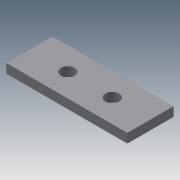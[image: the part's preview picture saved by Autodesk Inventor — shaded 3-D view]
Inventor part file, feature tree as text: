
AUTODESK INVENTOR PART (.ipt)
format: ipt  version: 2013 (Build 170138000, 138)  size: 76,800 bytes
history: native  units: mm
features: extrude x1, sketch x1
ambient origin geometry x8: Origin, YZ Plane, XZ Plane, XY Plane, X Axis, Y Axis, Z Axis, Center Point
bodies: Solid1 (feature_tree)
feature tree (2):
  extrude  "Extrusion1"  Depth=50.0mm
  sketch  "Sketch1"  dims[d0=131.0mm d1=50.0mm d2=24.1mm d3=24.1mm d4=15.0mm d5=15.0mm d6=10.0mm d7=0.0mm]
